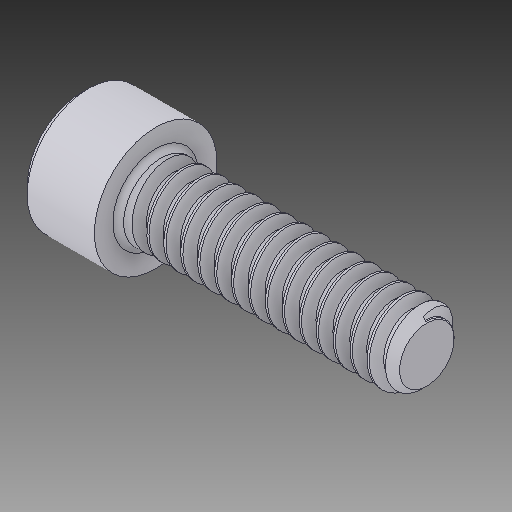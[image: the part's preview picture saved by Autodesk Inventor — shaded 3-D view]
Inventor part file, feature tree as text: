
AUTODESK INVENTOR PART (.ipt)
format: ipt  version: 2018 (Build 220112000, 112)  size: 638,464 bytes
history: native  units: in
note: dims shown in document units (in); Inventor stores cm internally (conversion verified against a paired STEP export)
features: thread x1
ambient origin geometry x8: Origin, YZ Plane, XZ Plane, XY Plane, X Axis, Y Axis, Z Axis, Center Point
bodies: Solid1 (feature_tree)
feature tree (1):
  thread  "Thread1"  [1 undecoded]
note: 1 required parameter value undecoded (feature->parameter linkage not recoverable at this tier; creation-order binding heuristic only, values carry confidence <= 0.55)
